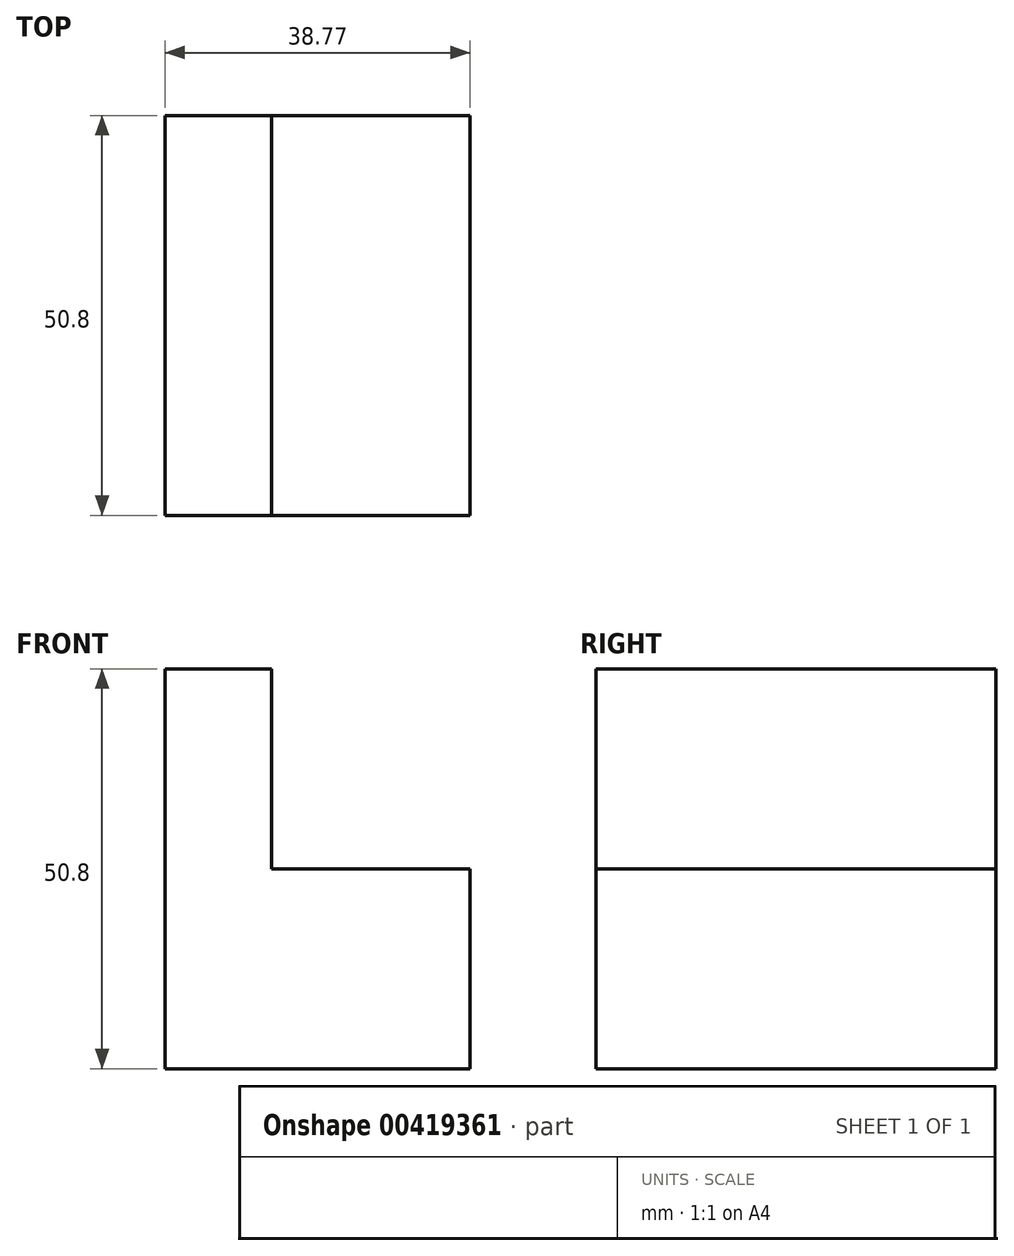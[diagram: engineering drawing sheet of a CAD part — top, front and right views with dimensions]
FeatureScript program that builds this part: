
annotation { "Feature Type Name" : "Feature", "Feature Type Description" : "" }
export const myFeature = defineFeature(function(context is Context, id is Id, definition is map)
    precondition{}
    {
        {
            var Q0;
            Q0=qCreatedBy(makeId("Front.planeOp"),FACE);
            var sketch = newSketch(context, id + "F0", { "sketchPlane" : qUnion([Q0])});
            skLineSegment(sketch, "E0", {"start": v(0, 0) * mm, "end": v(-50.8, 0) * mm});
            skLineSegment(sketch, "E1", {"start": v(-50.8, 0) * mm, "end": v(-50.8, 50.8) * mm});
            skLineSegment(sketch, "E2", {"start": v(-50.8, 50.8) * mm, "end": v(-37.24, 50.8) * mm});
            skLineSegment(sketch, "E3", {"start": v(-37.24, 50.8) * mm, "end": v(-37.24, 25.4) * mm});
            skLineSegment(sketch, "E4", {"start": v(-37.24, 25.4) * mm, "end": v(-12.03, 25.4) * mm});
            skLineSegment(sketch, "E5", {"start": v(-12.03, 25.4) * mm, "end": v(-12.03, 0) * mm});
            skSolve(sketch);
        }
        {
            var Q0;
            Q0 = qSketchRegion(id + "F0", true);
            extrude(context, id + "F1", {"entities" : qUnion([Q0]), "depth" : 50.8 * mm});
        }
    });
